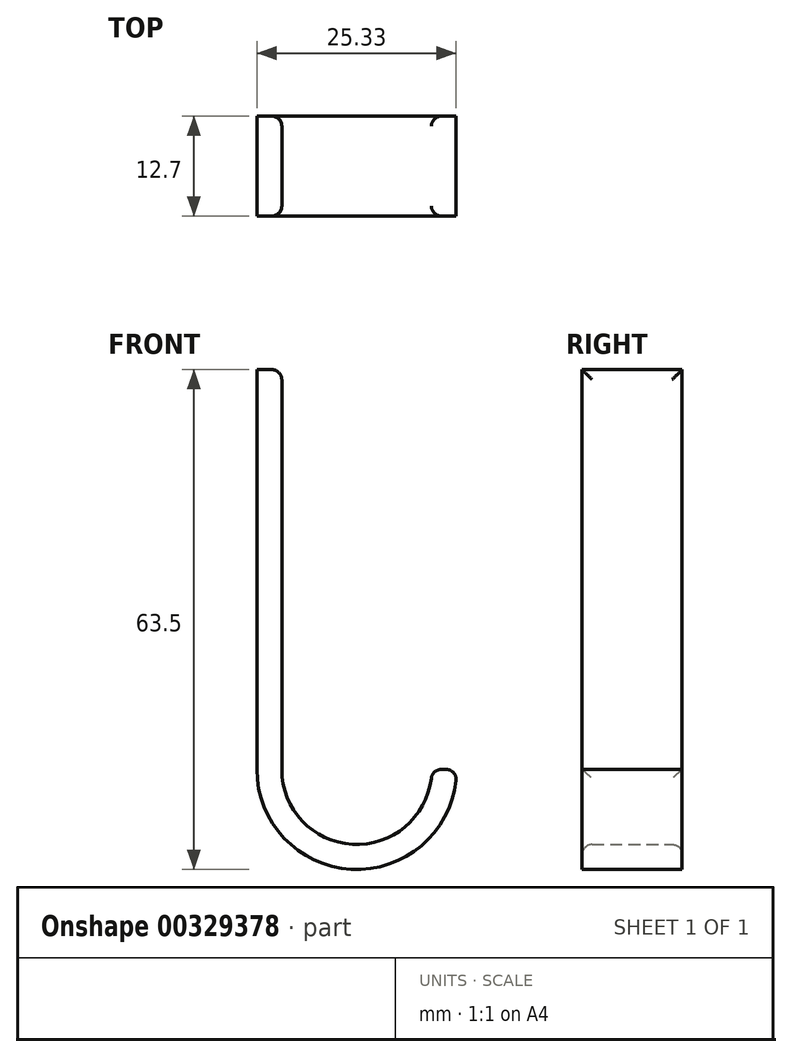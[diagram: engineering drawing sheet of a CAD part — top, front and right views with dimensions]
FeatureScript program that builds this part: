
annotation { "Feature Type Name" : "Feature", "Feature Type Description" : "" }
export const myFeature = defineFeature(function(context is Context, id is Id, definition is map)
    precondition{}
    {
        {
            var Q0;
            Q0=qCreatedBy(makeId("Front.planeOp"),FACE);
            var sketch = newSketch(context, id + "F0", { "sketchPlane" : qUnion([Q0])});
            skLineSegment(sketch, "E0", {"start": v(-60.67, 68.87) * mm, "end": v(-60.67, 18.07) * mm});
            skArc(sketch, "E1", {"start": v(-60.67, 18.07) * mm, "mid": v(-51.14, 8.54) * mm, "end": v(-41.62, 18.07) * mm});
            skArc(sketch, "E2.0", {"start": v(-63.84, 18.07) * mm, "mid": v(-51.14, 5.37) * mm, "end": v(-38.44, 18.07) * mm});
            skLineSegment(sketch, "E2.1", {"start": v(-63.84, 68.87) * mm, "end": v(-63.84, 18.07) * mm});
            skLineSegment(sketch, "E3", {"start": v(-63.84, 68.87) * mm, "end": v(-60.67, 68.87) * mm});
            skLineSegment(sketch, "E4", {"start": v(-41.62, 18.07) * mm, "end": v(-38.44, 18.07) * mm});
            skSolve(sketch);
        }
        {
            var Q0;
            Q0=makeQuery(id+"F0.imprint","IMPRINT",FACE,{"disambiguationData":[TD([[makeQuery(id+"F0.imprint","IMPRINT",EDGE,{"derivedFrom":sQuery(id+"F0.wireOp",EDGE,"E0")}),-1.0]])]});
            extrude(context, id + "F1", {"entities" : qUnion([Q0]), "depth" : 12.7 * mm});
        }
        {
            var Q0;
            Q0=makeQuery(id+"F1.opExtrude","CAP_EDGE",EDGE,{"disambiguationData":[OSD([sQuery(id+"F0.wireOp",EDGE,"E0")])],"isStart":false});
            var Q1;
            Q1=makeQuery(id+"F1.opExtrude","CAP_EDGE",EDGE,{"disambiguationData":[OSD([sQuery(id+"F0.wireOp",EDGE,"E0")])],"isStart":true});
            var Q2;
            Q2=makeQuery(id+"F1.opExtrude","SWEPT_EDGE",EDGE,{"disambiguationData":[OSD([sQuery(id+"F0.wireOp",EDGE,"E2.0"),sQuery(id+"F0.wireOp",EDGE,"E4")])]});
            var Q3;
            Q3=makeQuery(id+"F1.opExtrude","SWEPT_EDGE",EDGE,{"disambiguationData":[OSD([sQuery(id+"F0.wireOp",EDGE,"E1"),sQuery(id+"F0.wireOp",EDGE,"E4")])]});
            var Q4;
            Q4=makeQuery(id+"F1.opExtrude","SWEPT_EDGE",EDGE,{"disambiguationData":[OSD([sQuery(id+"F0.wireOp",EDGE,"E0"),sQuery(id+"F0.wireOp",EDGE,"E3")])]});
            fillet(context, id + "F2", {"entities" : qUnion([Q0, Q1, Q2, Q3, Q4]), "radius" : 1.27 * mm, "tangentPropagation" : true, "allowEdgeOverflow" : false});
        }
    });
